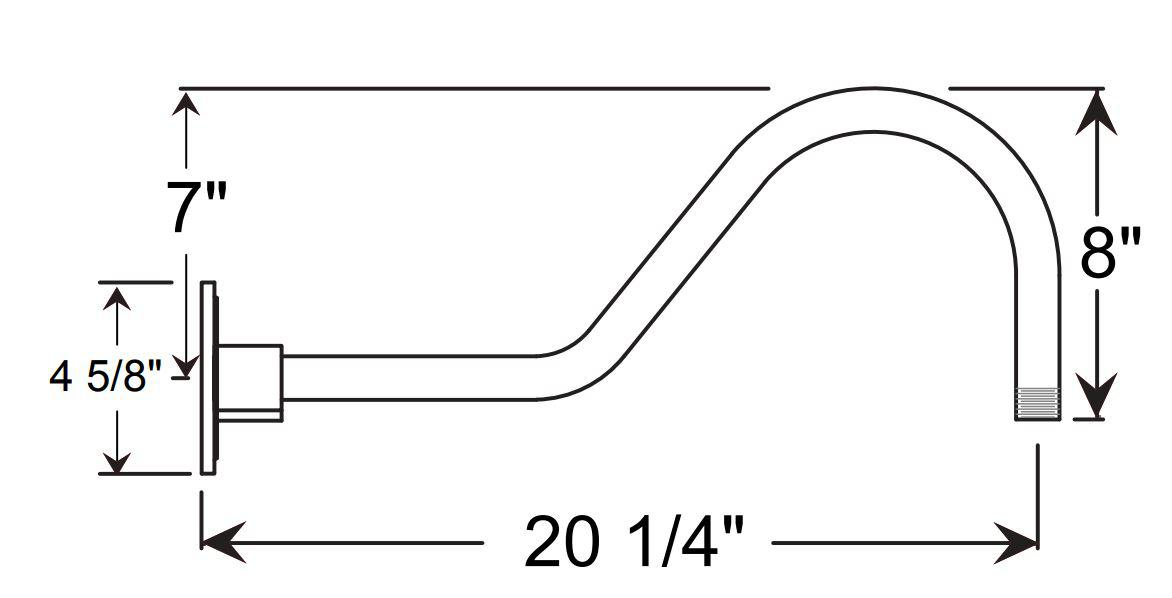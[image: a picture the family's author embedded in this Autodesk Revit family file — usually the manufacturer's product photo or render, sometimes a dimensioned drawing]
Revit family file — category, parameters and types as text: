
# Revit family: Vintage Angle AU8 12,14
name_source: partatom
category: Lighting Fixtures
units: mm (PartAtom-declared; Revit-internal decimal feet)

## family parameters
Always vertical = Yes
Cut with Voids When Loaded = No
Light Source = Yes
OmniClass Number = 23.80.70.00
OmniClass Title = Lighting
Part Type = Normal
Room Calculation Point = No
Round Connector Dimension = Use Diameter
Shared = No
Work Plane-Based = No

## types (2) — shared parameters
Apparent Load = 200 VA
Body Colour = Spun aluminium
Body Material = body
CRI = >90
Canopy Body = LILAC
Color Filter = 16777215
Construction Material = Heavy Duty spun aluminum.
Default Elevation = 0' - 0"
Description = 120-277 Voltage
Dimming = 1%
Dimming Lamp Color Temperature Shift = <None>
Efficiency = 65-125 lumens per watt
HUB = Steel, Paint Finish, Dark Gray, Matte
Lamp = INC
Life = L70 50,000 hours
Load Classification = Lighting
Manufacturer = ANP Lighting
Photometric Web File = generic
Power Factor = 1
Tilt Angle = 90.00°
URL = https://www.anplighting.com
Voltage = 120 V
Warranty = 5 year limited warranty
Wattage Comments = 200W
b = 0' - 3"

## per-type parameters (varying)
| type | AU812 | AU814 | Fixture Diameter | Fixture Height | Weight | a |
| AU812 | Yes | No | 1' - 0" | 1' - 0 1/4" | 2.0lb | 0' - 9" |
| AU814 | No | Yes | 1' - 2" | 1' - 2" | 3.0lb | 0' - 10" |

note: column(s) folded — value = type name in every type: Model

## geometry (parser evidence)
native form markers: Sweep x28
no freeform markers — native parametric forms only
